# Revit family: led-e-a60-fila-e27-4_5w-dim-2700k-fr_500010001900_faed
name_source: partatom
category: Leuchten
revit_build: Autodesk Revit 2016 (Build: 20190508_0715(x64)
units: mm (PartAtom-declared; Revit-internal decimal feet)

## family parameters
Basisbauteil = Fläche
Beim Laden mit Abzugskörper schneiden = Nein
Bemaßung runder Anschluss = Durchmesser verwenden
Gemeinsam genutzt = Nein
Lichtquelle = Nein
Raumberechnungspunkt = Nein
Teiletyp = Normal

## types (1)
- LED-E-A60-FILA-E27-4.5W-DIM-2700K-FR (1 x LED, 442 lm)
    Approval mark = CE
    Beschreibung = Classic light bulb shape ensures an easy replacement. Instant 100% light when switched on and no startup time. No UV / IR radiance so there is less risk of damage. Up to 86% less energy consumption than traditional bulbs.
    CIE Flux Codes = 19 43 70 50 99
    Height = 105 mm
    Hersteller = OPPLE
    Lamp Light Flux = 442 lm
    Lamp count = 1
    Lampe = 1 x LED
    Length = 60 mm  [stored 0.19685 ft]
    Luminous efficacy = 91 lm/W
    ModVariant = Nein
    Modell = 500010001900
    Mounting Place = Ceiling
    Mounting Type = Surface mounted
    Number of Poles = 1
    OnlyDefault = Ja
    Power Factor = 1
    Product Name = LED-E-A60-FILA-E27-4.5W-DIM-2700K-FR
    Product group = Filament A60
    ProductGroupID = 310
    Protection Class = Protection class I
    Protection Degree = IP 20
    RLX_Detail_Level = 1
    RlxData = <blob elided: 20313 chars, md5=70082b29>
    Scheinlast = 5 VA
    Socket = socket
    Standby Power = 0 W
    System Light Flux = 438 lm
    System Power = 5 W
    Typenbild = 500010001900.jpg
    Typenkommentare = Product without accessories
    URL = http://relux.com
    VarID = ---
    Voltage = 0 V
    Vorgabe-Ansicht = 1800 mm
    Weight = 0.00 kg
    Width = 60 mm  [stored 0.19685 ft]

note: [stored X ft] marks values corroborated as IEEE doubles in the binary element streams (Revit-internal decimal feet)

## geometry (parser evidence)
native form markers: Blend x4, Sweep x13
no freeform markers — native parametric forms only
